# Revit family: gorter_RHTX_1010
name_source: partatom
category: Windows
units: mm (PartAtom-declared; Revit-internal decimal feet)

## family parameters
Always vertical = No
Cut with Voids When Loaded = No
Host = Roof
Room Calculation Point = No
Shared = Yes

## types (3) — shared parameters
A = 1000 mm  [stored 3.28084 ft]
Analytic Construction = <None>
Belastbaarheid = 1050 kg/m2
Bestendigheid tegen windbelasting = 3000 Pa
Constructiesterkte = ± 3000 Pa
Geluidwerendheid = 26 dB
Hard body impact test (EN 356) = Class P5A
Hatch Material = Gorter_Material 1
Manufacturer = Gorter
Model = RHTX
Oppervlaktebehandeling binnenzijde = Gepoedercoat RAL9010
Oppervlaktebehandeling buitenzijde = Gepoedercoat RAL7047
Rough Width = 1000 mm  [stored 3.28084 ft]
Soft body impact test (EN 13049) = Class 5
URL = http://www.gortergroup.com
Width = 1000 mm  [stored 3.28084 ft]
Wind- en waterdichtheid = 650 Pa

## per-type parameters (varying)
| type | B | Height | Rough Height | Weight (kg) |
| RHTX1010 | 1000 mm  [stored 3.28084 ft] | 1000 mm  [stored 3.28084 ft] | 1000 mm  [stored 3.28084 ft] | 58 |
| RHTX1020 | 2000 mm  [stored 6.56168 ft] | 2000 mm  [stored 6.56168 ft] | 2000 mm  [stored 6.56168 ft] | 87 |
| RHTX1015 | 1500 mm  [stored 4.92126 ft] | 1500 mm  [stored 4.92126 ft] | 1500 mm  [stored 4.92126 ft] | 72 |

note: [stored X ft] marks values corroborated as IEEE doubles in the binary element streams (Revit-internal decimal feet)

## geometry (parser evidence)
native form markers: Sweep x2
no freeform markers — native parametric forms only
